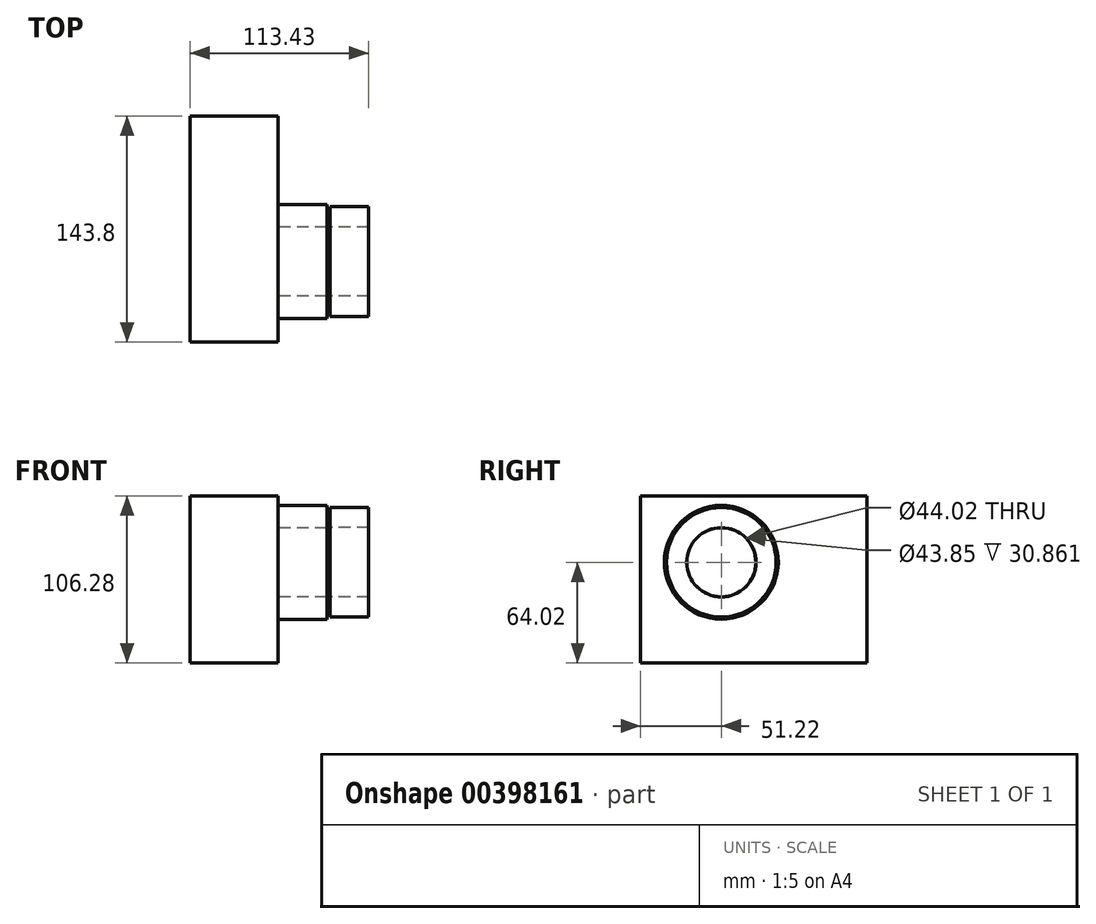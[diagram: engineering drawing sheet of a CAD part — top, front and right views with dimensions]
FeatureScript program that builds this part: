
annotation { "Feature Type Name" : "Feature", "Feature Type Description" : "" }
export const myFeature = defineFeature(function(context is Context, id is Id, definition is map)
    precondition{}
    {
        {
            var Q0;
            Q0=qCreatedBy(makeId("Front.planeOp"),FACE);
            var sketch = newSketch(context, id + "F0", { "sketchPlane" : qUnion([Q0])});
            skLineSegment(sketch, "E0", {"start": v(0, 21.93) * mm, "end": v(31.01, 21.93) * mm});
            skLineSegment(sketch, "E1", {"start": v(31.01, 21.93) * mm, "end": v(31.01, 36.15) * mm});
            skLineSegment(sketch, "E2", {"start": v(31.01, 36.15) * mm, "end": v(0, 36.15) * mm});
            skLineSegment(sketch, "E3", {"start": v(0, 36.15) * mm, "end": v(0, 21.93) * mm});
            skSolve(sketch);
        }
        {
            var Q0;
            Q0=qCreatedBy(makeId("Front.planeOp"),FACE);
            var sketch = newSketch(context, id + "F1", { "sketchPlane" : qUnion([Q0])});
            skLineSegment(sketch, "E4.bottom", {"start": v(32.79, 34.83) * mm, "end": v(57.43, 34.83) * mm});
            skLineSegment(sketch, "E4.top", {"start": v(32.79, 22) * mm, "end": v(57.43, 22) * mm});
            skLineSegment(sketch, "E4.left", {"start": v(32.79, 34.83) * mm, "end": v(32.79, 22) * mm});
            skLineSegment(sketch, "E4.right", {"start": v(57.43, 34.83) * mm, "end": v(57.43, 22) * mm});
            skSolve(sketch);
        }
        {
            var Q0;
            Q0=qCreatedBy(makeId("Front.planeOp"),FACE);
            var sketch = newSketch(context, id + "F2", { "sketchPlane" : qUnion([Q0])});
            skLineSegment(sketch, "E5", {"start": v(0, 0) * mm, "end": v(50.38, 0) * mm, "construction": true});
            skSolve(sketch);
        }
        {
            var Q0;
            Q0 = qSketchRegion(id + "F0", true);
            var Q1;
            Q1=sQuery(id+"F2.wireOp",EDGE,"E5");
            revolve(context, id + "F3", {"entities" : qUnion([Q0]), "axis" : qUnion([Q1]), "revolveType" : RevolveType.FULL});
        }
        {
            var Q0;
            Q0=makeQuery(id+"F3.opRevolve","SWEPT_EDGE",EDGE,{"disambiguationData":[OSD([sQuery(id+"F0.wireOp",EDGE,"E0"),sQuery(id+"F0.wireOp",EDGE,"E1")])]});
            chamfer(context, id + "F4", {"entities" : qUnion([Q0]), "width" : 0.15 * mm, "tangentPropagation" : true});
        }
        {
            var Q0;
            Q0 = qSketchRegion(id + "F1", true);
            var Q1;
            Q1=sQuery(id+"F2.wireOp",EDGE,"E5");
            revolve(context, id + "F5", {"operationType" : NewBodyOperationType.ADD, "entities" : qUnion([Q0]), "axis" : qUnion([Q1]), "revolveType" : RevolveType.FULL});
        }
        {
            var Q0;
            Q0=qCreatedBy(makeId("Right.planeOp"),FACE);
            var sketch = newSketch(context, id + "F6", { "sketchPlane" : qUnion([Q0])});
            skLineSegment(sketch, "E6.bottom", {"start": v(92.58, 42.26) * mm, "end": v(-51.22, 42.26) * mm});
            skLineSegment(sketch, "E6.top", {"start": v(92.58, -64.02) * mm, "end": v(-51.22, -64.02) * mm});
            skLineSegment(sketch, "E6.left", {"start": v(92.58, 42.26) * mm, "end": v(92.58, -64.02) * mm});
            skLineSegment(sketch, "E6.right", {"start": v(-51.22, 42.26) * mm, "end": v(-51.22, -64.02) * mm});
            skSolve(sketch);
        }
        {
            var Q0;
            Q0 = qSketchRegion(id + "F6", true);
            extrude(context, id + "F7", {"entities" : qUnion([Q0]), "operationType" : NewBodyOperationType.ADD, "oppositeDirection" : true, "depth" : 56 * mm});
        }
    });
